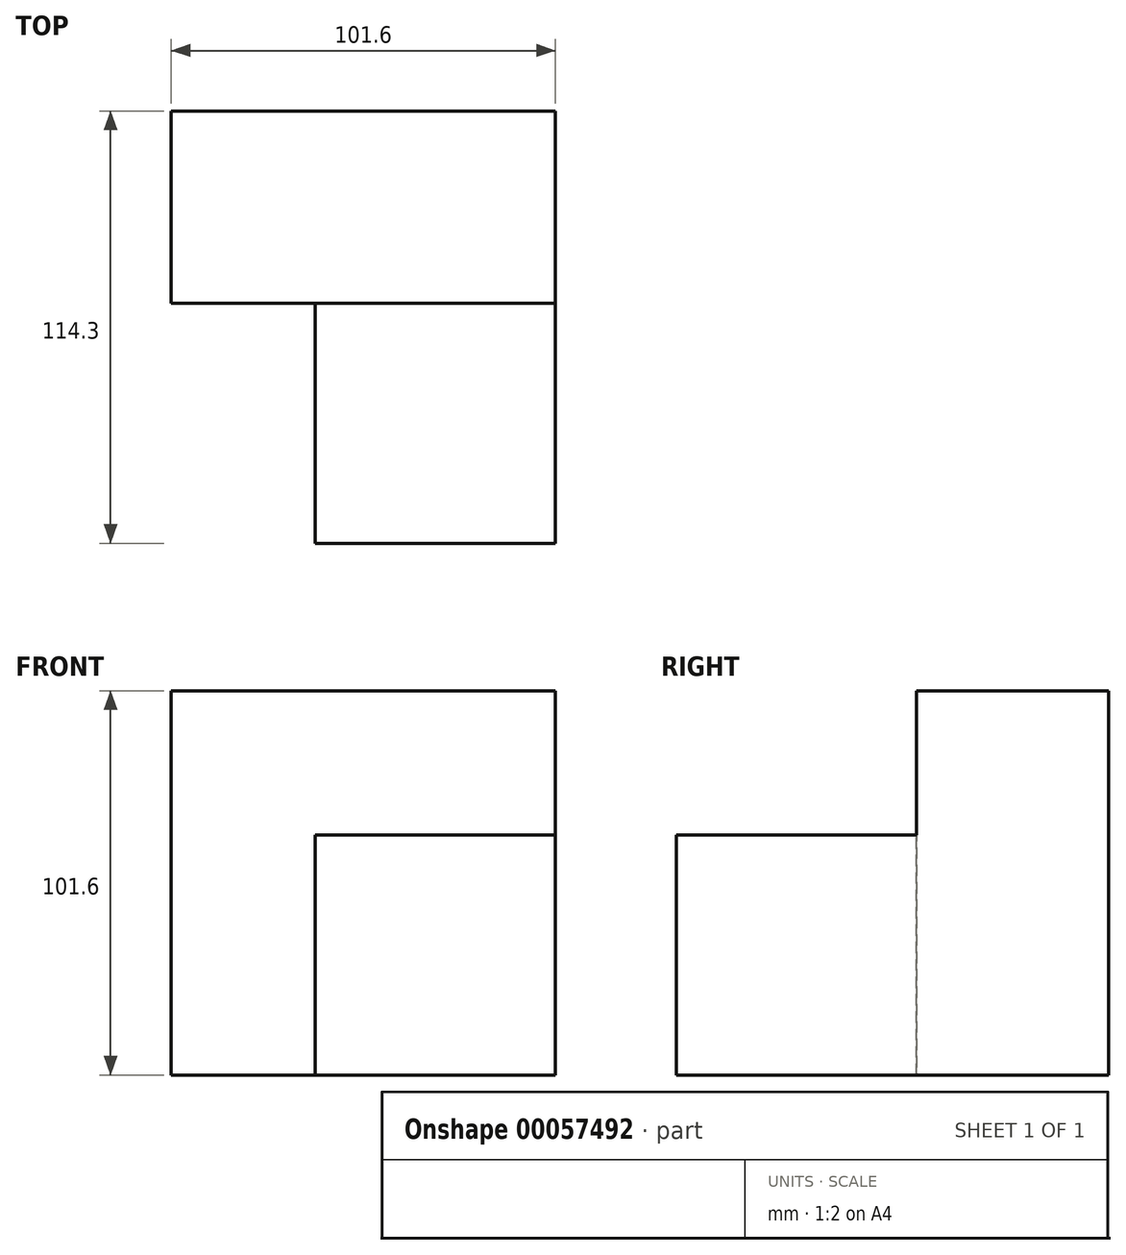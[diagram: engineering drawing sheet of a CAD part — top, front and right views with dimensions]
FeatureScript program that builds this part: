
annotation { "Feature Type Name" : "Feature", "Feature Type Description" : "" }
export const myFeature = defineFeature(function(context is Context, id is Id, definition is map)
    precondition{}
    {
        {
            var Q0;
            Q0=qCreatedBy(makeId("Top.planeOp"),FACE);
            var sketch = newSketch(context, id + "F0", { "sketchPlane" : qUnion([Q0])});
            skLineSegment(sketch, "E0.bottom", {"start": v(-50.8, 25.4) * mm, "end": v(50.8, 25.4) * mm});
            skLineSegment(sketch, "E0.top", {"start": v(-50.8, -25.4) * mm, "end": v(50.8, -25.4) * mm});
            skLineSegment(sketch, "E0.left", {"start": v(-50.8, 25.4) * mm, "end": v(-50.8, -25.4) * mm});
            skLineSegment(sketch, "E0.right", {"start": v(50.8, 25.4) * mm, "end": v(50.8, -25.4) * mm});
            skSolve(sketch);
        }
        {
            var Q0;
            Q0=makeQuery(id+"F0.imprint","IMPRINT",FACE,{"disambiguationData":[TD([[makeQuery(id+"F0.imprint","IMPRINT",EDGE,{"derivedFrom":sQuery(id+"F0.wireOp",EDGE,"E0.bottom")}),-1.0]])]});
            extrude(context, id + "F1", {"entities" : qUnion([Q0]), "depth" : 101.6 * mm});
        }
        {
            var Q0;
            Q0=makeQuery(id+"F1.opExtrude","SWEPT_FACE",FACE,{"disambiguationData":[OSD([sQuery(id+"F0.wireOp",EDGE,"E0.top")])]});
            var sketch = newSketch(context, id + "F2", { "sketchPlane" : qUnion([Q0])});
            skLineSegment(sketch, "E1.0", {"start": v(50.8, 101.6) * mm, "end": v(50.8, 0) * mm, "construction": true});
            skLineSegment(sketch, "E2.0", {"start": v(-50.8, 0) * mm, "end": v(50.8, 0) * mm, "construction": true});
            skLineSegment(sketch, "E3.bottom", {"start": v(50.8, 0) * mm, "end": v(-12.7, 0) * mm});
            skLineSegment(sketch, "E3.top", {"start": v(50.8, 63.5) * mm, "end": v(-12.7, 63.5) * mm});
            skLineSegment(sketch, "E3.left", {"start": v(50.8, 0) * mm, "end": v(50.8, 63.5) * mm});
            skLineSegment(sketch, "E3.right", {"start": v(-12.7, 0) * mm, "end": v(-12.7, 63.5) * mm});
            skSolve(sketch);
        }
        {
            var Q0;
            Q0=makeQuery(id+"F2.imprint","IMPRINT",FACE,{"disambiguationData":[TD([[makeQuery(id+"F2.imprint","IMPRINT",EDGE,{"derivedFrom":sQuery(id+"F2.wireOp",EDGE,"E3.bottom")}),1.0]])]});
            var Q1;
            Q1 = qSketchRegion(id + "F2", true);
            extrude(context, id + "F3", {"entities" : qUnion([Q0, Q1]), "operationType" : NewBodyOperationType.ADD, "depth" : 63.5 * mm});
        }
    });
